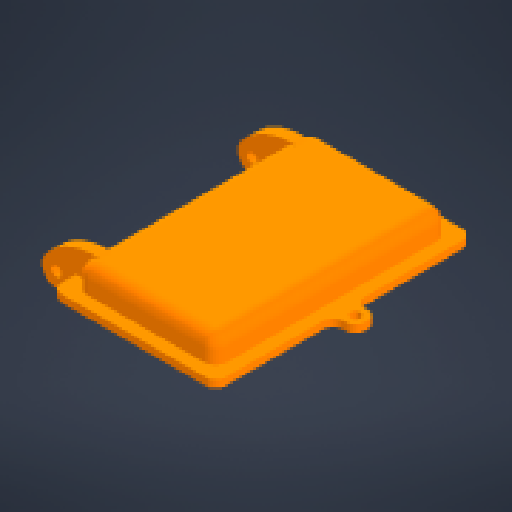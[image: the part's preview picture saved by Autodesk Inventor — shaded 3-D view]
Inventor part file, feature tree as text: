
AUTODESK INVENTOR PART (.ipt)
format: ipt  version: 2024 (Build 280153000, 153)  size: 296,960 bytes
history: native  units: mm
features: reference x17, other x6, extrude x5, sketch x5, fillet x2, chamfer x1, shell x1, mirror x1, projected_geometry x1
ambient origin geometry x8: Origin, YZ Plane, XZ Plane, XY Plane, X Axis, Y Axis, Z Axis, Center Point
bodies: Body1 (feature_tree)
feature tree (39):
  other  "Твердое тело1"
  extrude  "Выдавливание1"  Depth=2.0mm
  chamfer  "Фаска1"  Distance=2.0mm
  extrude  "Выдавливание2"  Depth=1.0mm TaperAngle=45.0deg
  extrude  "Выдавливание3"  Depth=3.0mm TaperAngle=0.0deg
  fillet  "Сопряжение1"  Radius=5.0mm
  other  "РабПлоскость1"
  other  "РабПлоскость2"
  shell  "Оболочка1"  Thickness=10.25mm
  extrude  "Выдавливание5"  Depth=5.0mm
  mirror  "Зеркальное отражение2"
  extrude  "Выдавливание6"  Depth=4.0mm
  fillet  "Сопряжение2"  Radius=4.0mm
  sketch  "Эскиз1"
  reference  "Ссылка1"
  reference  "Ссылка2"
  reference  "Ссылка3"
  reference  "Ссылка4"
  reference  "Ссылка5"
  reference  "Ссылка6"
  reference  "Ссылка7"
  reference  "Ссылка8"
  sketch  "Эскиз2"
  reference  "Ссылка9"
  reference  "Ссылка10"
  reference  "Ссылка11"
  reference  "Ссылка12"
  reference  "Ссылка13"
  reference  "Ссылка15"
  reference  "Ссылка16"
  sketch  "Эскиз3"
  projected_geometry  "Спроецированная петля2"
  sketch  "Эскиз5"
  sketch  "Эскиз6"
  reference  "Ссылка17"
  reference  "Ссылка18"
  parser-record x1  (decoder bookkeeping rows leaked as tree rows — omitted from the tree; the rows remain in map.json)
  other  "back_box_asembly.iam"
  other  "back_box:1"
note: 1 file-system path scrubbed to <path> (originals preserved in map.json)
